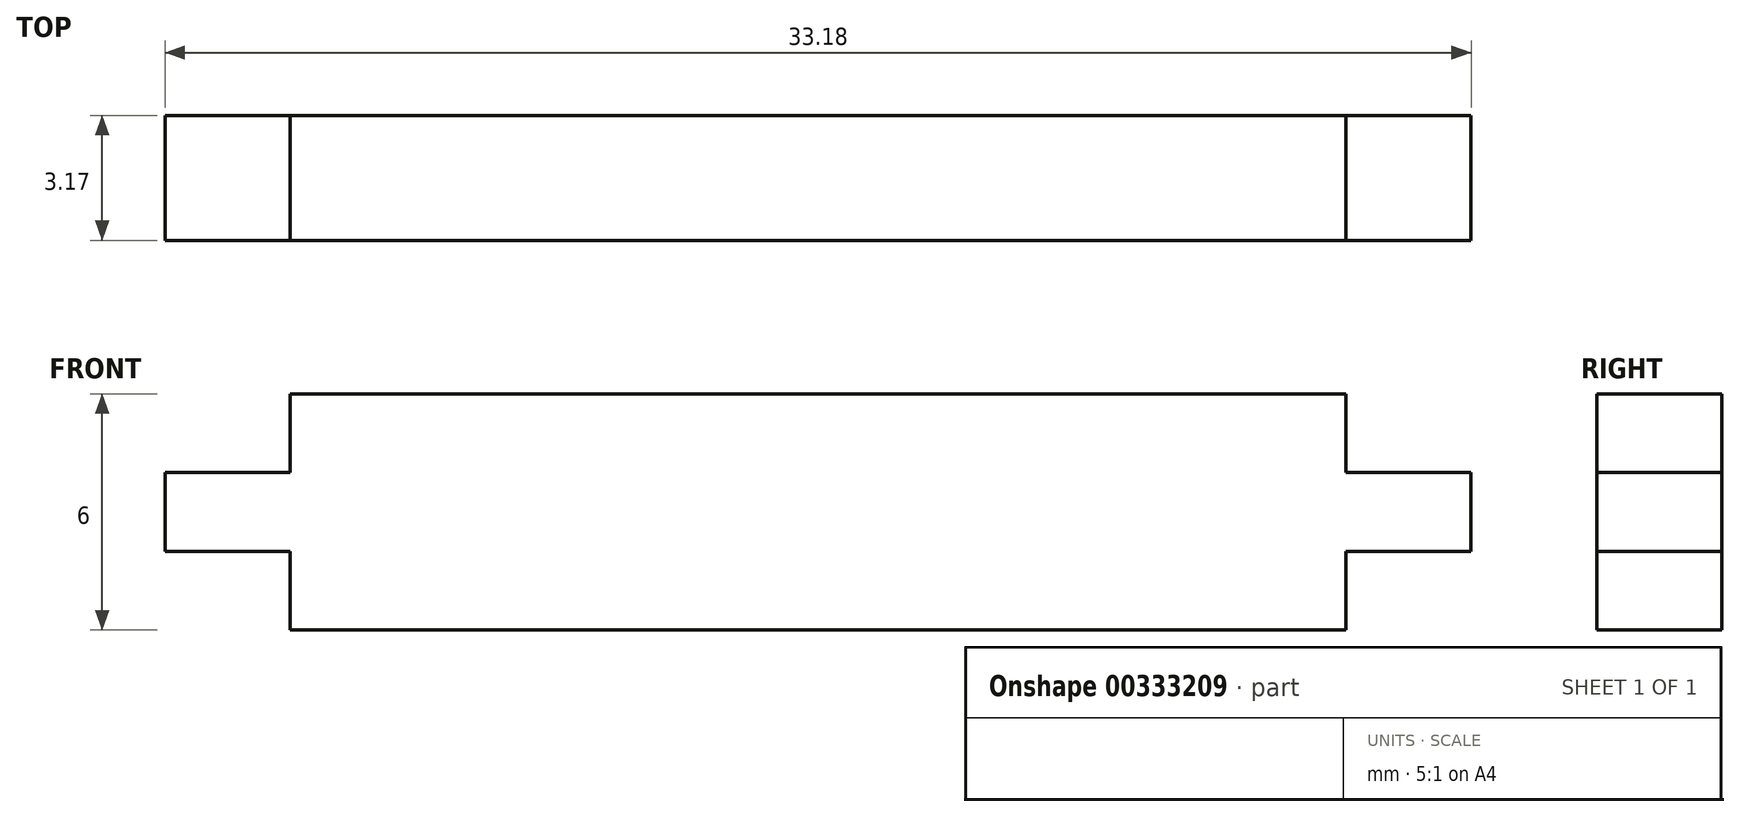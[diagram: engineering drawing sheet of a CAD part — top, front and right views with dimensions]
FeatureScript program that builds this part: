
annotation { "Feature Type Name" : "Feature", "Feature Type Description" : "" }
export const myFeature = defineFeature(function(context is Context, id is Id, definition is map)
    precondition{}
    {
        {
            var Q0;
            Q0=qCreatedBy(makeId("Front.planeOp"),FACE);
            var sketch = newSketch(context, id + "F0", { "sketchPlane" : qUnion([Q0])});
            skLineSegment(sketch, "E0.bottom", {"start": v(16.59, -1) * mm, "end": v(-16.59, -1) * mm});
            skLineSegment(sketch, "E0.top", {"start": v(16.59, 1) * mm, "end": v(-16.59, 1) * mm});
            skLineSegment(sketch, "E0.left", {"start": v(16.59, -1) * mm, "end": v(16.59, 1) * mm});
            skLineSegment(sketch, "E0.right", {"start": v(-16.59, -1) * mm, "end": v(-16.59, 1) * mm});
            skPoint(sketch, "E0.middle", {"position": v(0, 0) * mm});
            skLineSegment(sketch, "E1", {"start": v(-13.41, 1) * mm, "end": v(-13.41, 3) * mm});
            skLineSegment(sketch, "E2", {"start": v(-13.41, 3) * mm, "end": v(13.41, 3) * mm});
            skLineSegment(sketch, "E3", {"start": v(13.41, 3) * mm, "end": v(13.41, 1) * mm});
            skLineSegment(sketch, "E4.MirrorCS", {"start": v(-13.41, -3) * mm, "end": v(13.41, -3) * mm});
            skLineSegment(sketch, "E5.MirrorCS", {"start": v(-13.41, -1) * mm, "end": v(-13.41, -3) * mm});
            skLineSegment(sketch, "E6.MirrorCS", {"start": v(13.41, -3) * mm, "end": v(13.41, -1) * mm});
            skSolve(sketch);
        }
        {
            var Q0;
            Q0=qSketchRegion(id+"F0",true);
            extrude(context, id + "F1", {"entities" : qUnion([Q0]), "depth" : 3.17 * mm});
        }
    });
